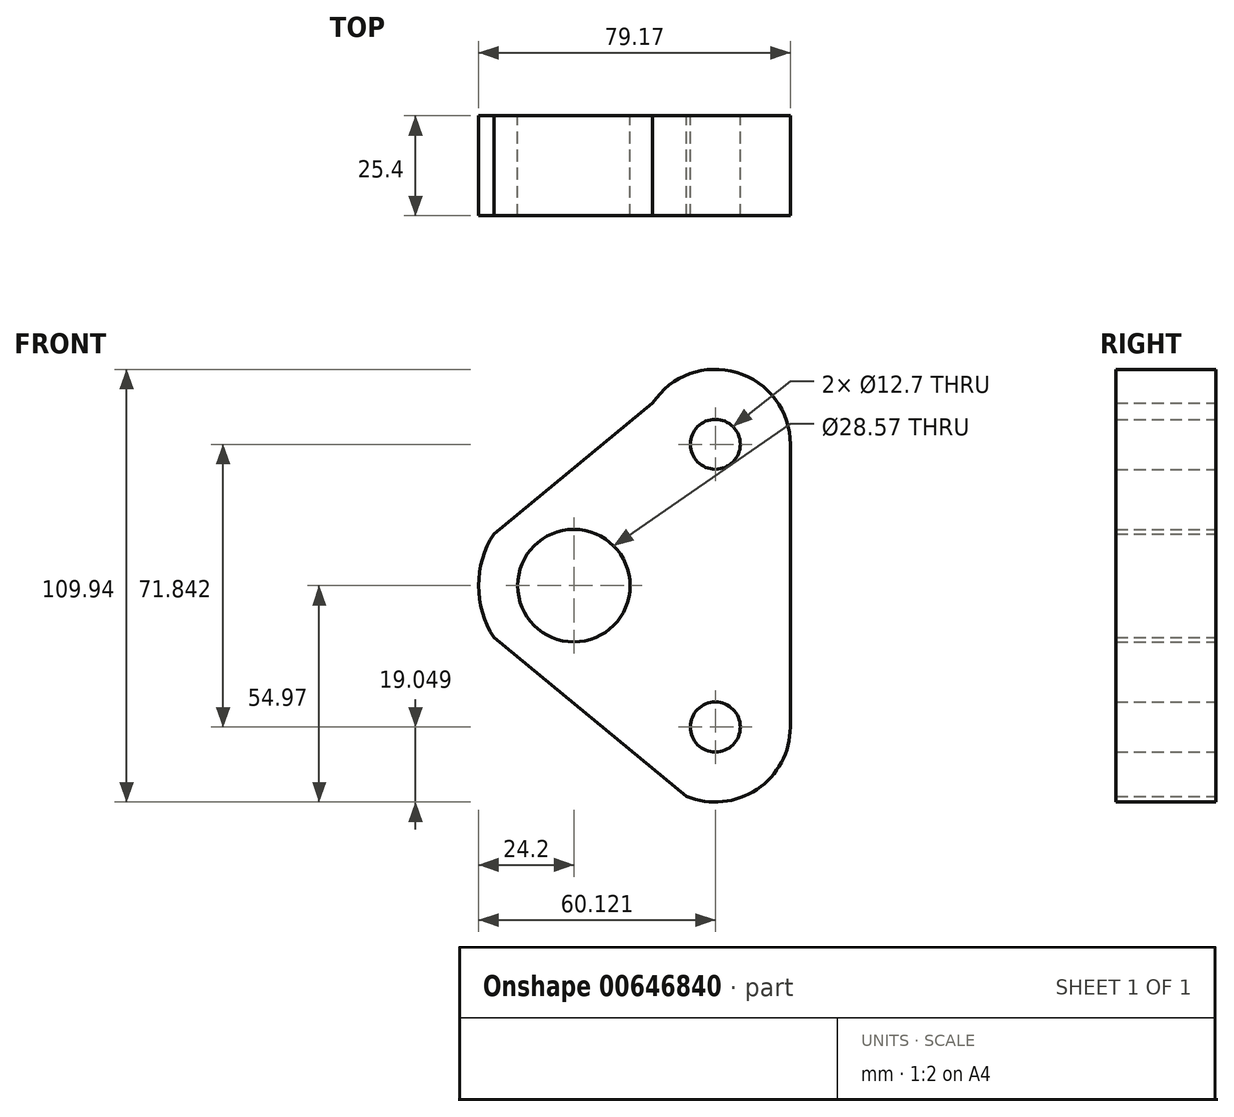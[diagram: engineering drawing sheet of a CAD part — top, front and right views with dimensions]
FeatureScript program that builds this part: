
annotation { "Feature Type Name" : "Feature", "Feature Type Description" : "" }
export const myFeature = defineFeature(function(context is Context, id is Id, definition is map)
    precondition{}
    {
        {
            var Q0;
            Q0=qCreatedBy(makeId("Front.planeOp"),FACE);
            var sketch = newSketch(context, id + "F0", { "sketchPlane" : qUnion([Q0])});
            skCircle(sketch, "E0", {"center": v(0, 0) * mm, "radius": 14.29 * mm});
            skCircle(sketch, "E1", {"center": v(35.92, -35.92) * mm, "radius": 6.35 * mm});
            skCircle(sketch, "E2", {"center": v(35.92, 35.92) * mm, "radius": 6.35 * mm});
            skArc(sketch, "E3", {"start": v(54.97, 35.92) * mm, "mid": v(41.4, 54.17) * mm, "end": v(20.02, 46.42) * mm});
            skArc(sketch, "E4", {"start": v(28.63, -53.52) * mm, "mid": v(46.5, -51.76) * mm, "end": v(54.97, -35.92) * mm});
            skLineSegment(sketch, "E5", {"start": v(54.97, 35.92) * mm, "end": v(54.97, -35.92) * mm});
            skLineSegment(sketch, "E6", {"start": v(28.63, -53.52) * mm, "end": v(-20.34, -13.1) * mm});
            skLineSegment(sketch, "E7", {"start": v(28.63, 53.52) * mm, "end": v(-20.34, 13.1) * mm});
            skArc(sketch, "E8.trimOffspring", {"start": v(-20.34, 13.1) * mm, "mid": v(-24.2, 0) * mm, "end": v(-20.34, -13.1) * mm});
            skLineSegment(sketch, "E9.trimOffspring", {"start": v(31.43, 31.43) * mm, "end": v(35.92, 35.92) * mm});
            skSolve(sketch);
        }
        {
            var Q0;
            Q0 = qSketchRegion(id + "F0", true);
            extrude(context, id + "F1", {"entities" : qUnion([Q0]), "depth" : 25.4 * mm, "offsetDistance" : 25.4 * mm});
        }
    });
